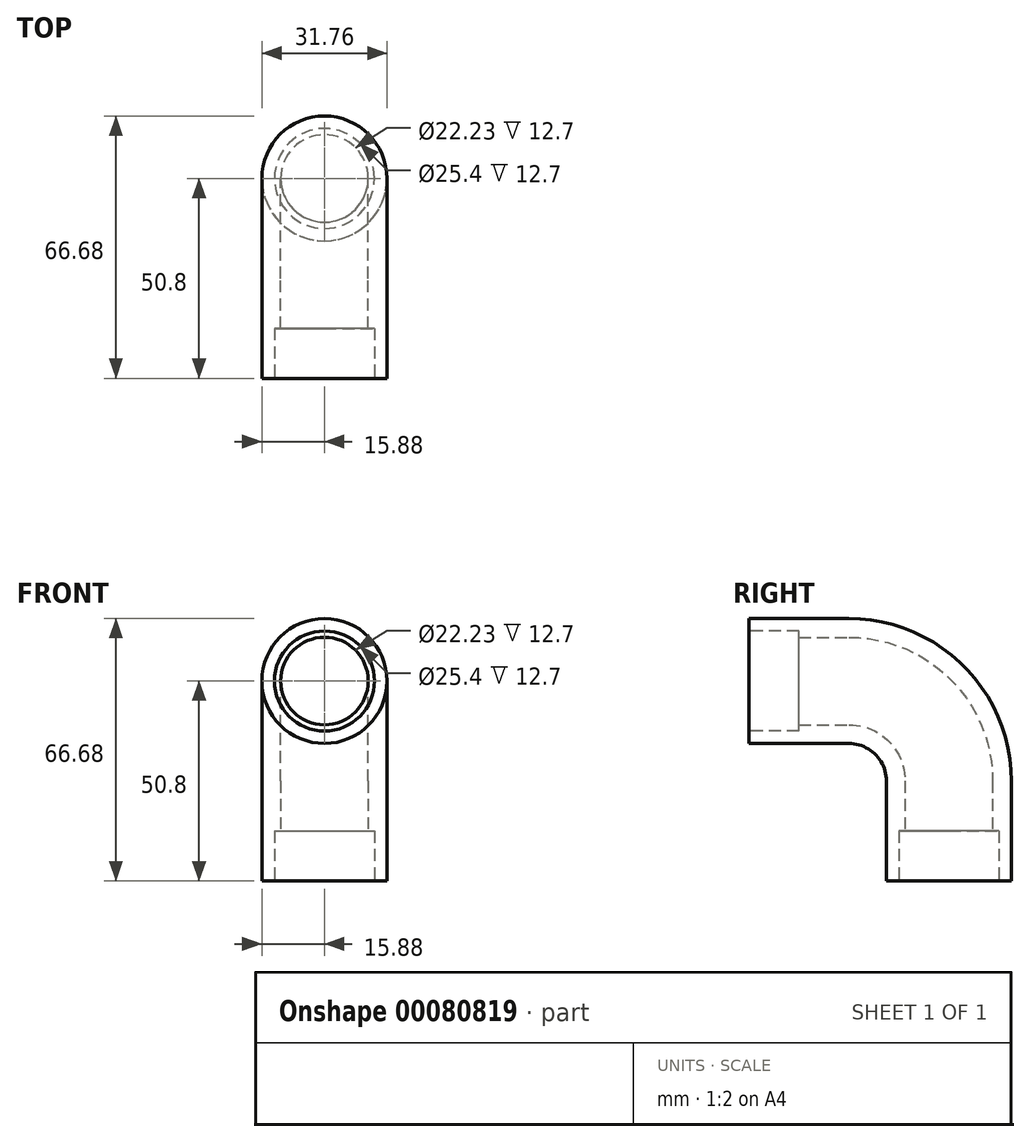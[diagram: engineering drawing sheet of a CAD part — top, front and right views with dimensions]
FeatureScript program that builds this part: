
annotation { "Feature Type Name" : "Feature", "Feature Type Description" : "" }
export const myFeature = defineFeature(function(context is Context, id is Id, definition is map)
    precondition{}
    {
        {
            var Q0;
            Q0=qCreatedBy(makeId("Front.planeOp"),FACE);
            var sketch = newSketch(context, id + "F0", { "sketchPlane" : qUnion([Q0])});
            skCircle(sketch, "E0", {"center": v(0, 0) * mm, "radius": 11.11 * mm});
            skCircle(sketch, "E1", {"center": v(0, 0) * mm, "radius": 15.88 * mm});
            skSolve(sketch);
        }
        {
            var Q0;
            Q0=qCreatedBy(makeId("Right.planeOp"),FACE);
            var sketch = newSketch(context, id + "F1", { "sketchPlane" : qUnion([Q0])});
            skPoint(sketch, "E2.visualSharp", {"position": v(74.33, 0) * mm});
            skLineSegment(sketch, "E3", {"start": v(0, 0) * mm, "end": v(25.4, 0) * mm});
            skLineSegment(sketch, "E4", {"start": v(50.8, -25.4) * mm, "end": v(50.8, -50.8) * mm});
            skPoint(sketch, "E5.visualSharp", {"position": v(50.8, 0) * mm});
            skArc(sketch, "E5.filletArc", {"start": v(50.8, -25.4) * mm, "mid": v(43.36, -7.44) * mm, "end": v(25.4, 0) * mm});
            skSolve(sketch);
        }
        {
            var Q0;
            Q0=makeQuery(id+"F0.imprint","IMPRINT",FACE,{"disambiguationData":[TD([[makeQuery(id+"F0.imprint","IMPRINT",EDGE,{"derivedFrom":sQuery(id+"F0.wireOp",EDGE,"E0")}),-1.0]])]});
            var Q1;
            Q1=sQuery(id+"F1.wireOp",EDGE,"E3");
            var Q2;
            Q2=sQuery(id+"F1.wireOp",EDGE,"E5.filletArc");
            var Q3;
            Q3=sQuery(id+"F1.wireOp",EDGE,"E4");
            sweep(context, id + "F2", {"profiles" : qUnion([Q0]), "path" : qUnion([Q1, Q2, Q3])});
        }
        {
            var Q0;
            Q0=qCreatedBy(makeId("Front.planeOp"),FACE);
            var sketch = newSketch(context, id + "F3", { "sketchPlane" : qUnion([Q0])});
            skCircle(sketch, "E6", {"center": v(0, 0) * mm, "radius": 12.7 * mm});
            skSolve(sketch);
        }
        {
            var Q0;
            Q0 = qSketchRegion(id + "F3", true);
            extrude(context, id + "F4", {"entities" : qUnion([Q0]), "operationType" : NewBodyOperationType.REMOVE, "oppositeDirection" : true, "depth" : 12.7 * mm});
        }
        {
            var Q0;
            Q0=makeQuery(id+"F2.opSweep","CAP_FACE",FACE,{"disambiguationData":[OSD([sQuery(id+"F0.wireOp",EDGE,"E0"),sQuery(id+"F0.wireOp",EDGE,"E1"),sQuery(id+"F1.wireOp",VERTEX,"E4.end")])],"isStart":false});
            var sketch = newSketch(context, id + "F5", { "sketchPlane" : qUnion([Q0])});
            skCircle(sketch, "E7", {"center": v(0, -50.8) * mm, "radius": 12.7 * mm});
            skSolve(sketch);
        }
        {
            var Q0;
            Q0 = qSketchRegion(id + "F5", true);
            extrude(context, id + "F6", {"entities" : qUnion([Q0]), "operationType" : NewBodyOperationType.REMOVE, "oppositeDirection" : true, "depth" : 12.7 * mm});
        }
    });
